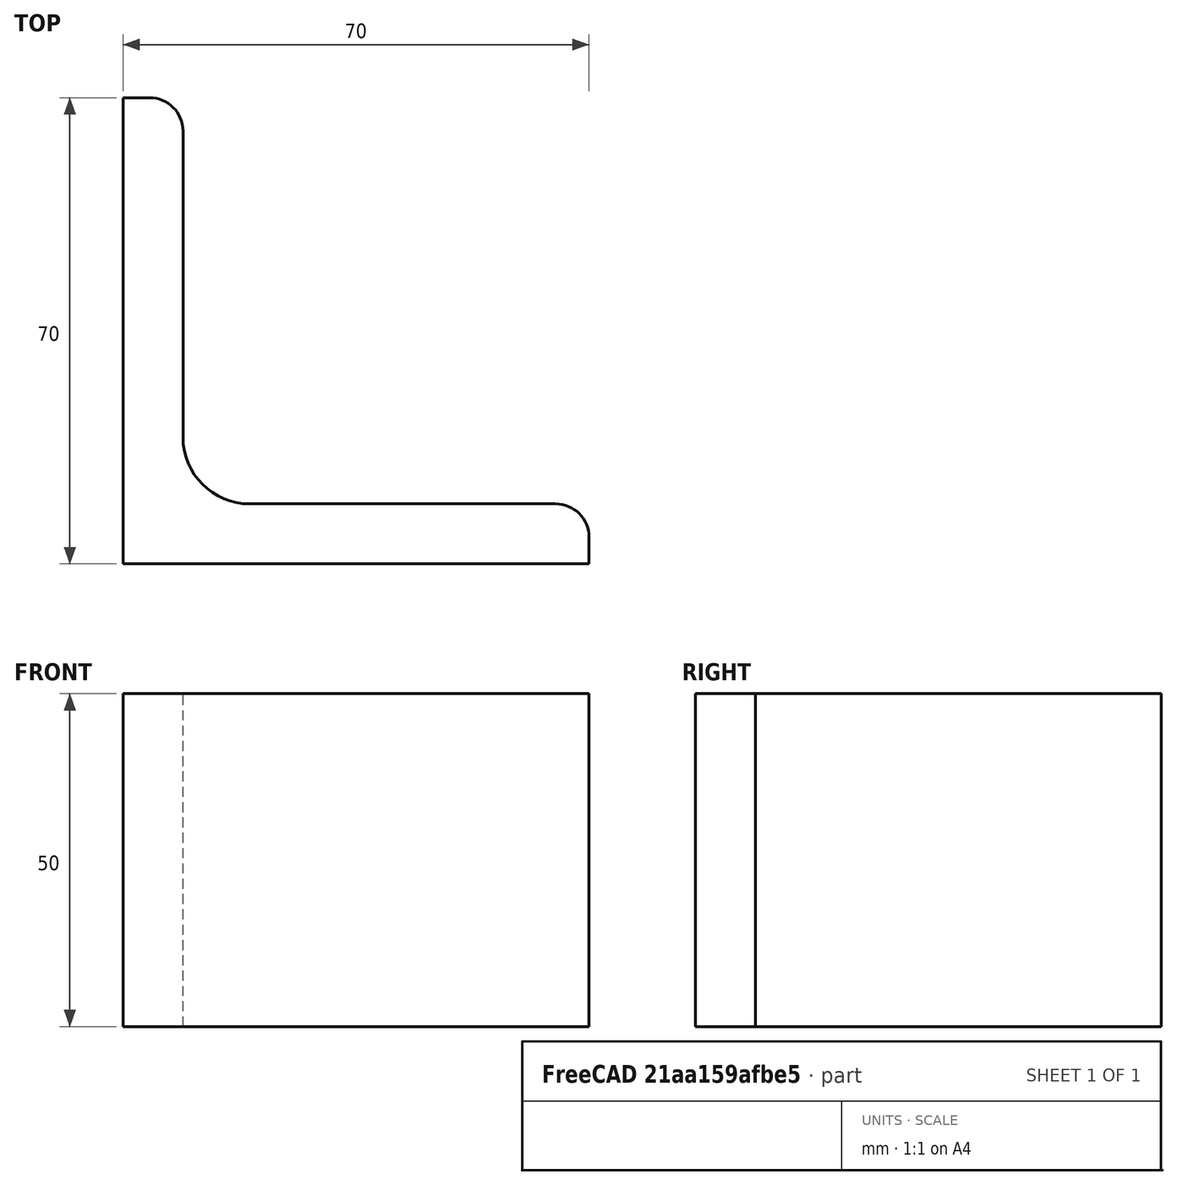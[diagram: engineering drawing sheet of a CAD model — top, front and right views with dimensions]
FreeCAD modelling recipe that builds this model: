
FCSTD DOCUMENT  (FreeCAD 0.15R4671 (Git))
Label: Angle Bar L70x70x9 EN10056 S235JR
License: All rights reserved
LicenseURL: http://en.wikipedia.org/wiki/All_rights_reserved
objects: Sketcher::SketchObject×1, Part::Extrusion×1
note: 2 computed .brp shape members not serialized (recipe doc carries the construction recipe); baked Part::Feature solids carry a one-line shape summary decoded from their .brp

FEATURE [Sketcher::SketchObject] Sketch
  sketch-geometry (9):
    g0: LineSegment StartX=0 StartY=0 StartZ=0 EndX=70 EndY=0 EndZ=0
    g1: LineSegment StartX=70 StartY=0 StartZ=0 EndX=70 EndY=4 EndZ=0
    g2: LineSegment StartX=65 StartY=9 StartZ=0 EndX=19 EndY=9 EndZ=0
    g3: LineSegment StartX=0 StartY=0 StartZ=0 EndX=0 EndY=70 EndZ=0
    g4: LineSegment StartX=0 StartY=70 StartZ=0 EndX=4 EndY=70 EndZ=0
    g5: LineSegment StartX=9 StartY=65 StartZ=0 EndX=9 EndY=19 EndZ=0
    g6: ArcOfCircle CenterX=19 CenterY=19 CenterZ=0 NormalX=0 NormalY=0 NormalZ=1 Radius=10 StartAngle=3.14159 EndAngle=4.71239
    g7: ArcOfCircle CenterX=4 CenterY=65 CenterZ=0 NormalX=0 NormalY=0 NormalZ=1 Radius=5 StartAngle=0 EndAngle=1.5708
    g8: ArcOfCircle CenterX=65 CenterY=4 CenterZ=0 NormalX=0 NormalY=0 NormalZ=1 Radius=5 StartAngle=0 EndAngle=1.5708
  constraints (23):
    c: Coincident(g0,g-1)
    c: Horizontal(g0)
    c: Coincident(g1,g0)
    c: Vertical(g1)
    c: Horizontal(g2)
    c: Coincident(g3,g-1)
    c: Vertical(g3)
    c: Coincident(g4,g3)
    c: Horizontal(g4)
    c: Vertical(g5)
    c: Tangent(g5,g6) = -1.5708
    c: Tangent(g2,g6) = 1.5708
    c: Tangent(g4,g7) = 1.5708
    c: Tangent(g5,g7) = 1.5708
    c: Tangent(g2,g8) = -1.5708
    c: Tangent(g1,g8) = -1.5708
    c: DistanceX(g0) = 70
    c: DistanceY(g3) = 70
    c: DistanceY(g0,g2) = 9
    c: DistanceX(g3,g5) = 9
    c: Radius(g6) = 10
    c: Radius(g8) = 5
    c: Radius(g7) = 5
FEATURE [Part::Extrusion] Extrude  label="Angle Bar L70x70x9 EN10056 S235JR"
  Base = -> Sketch
  Dir = (0,0,50)
  Solid = true
